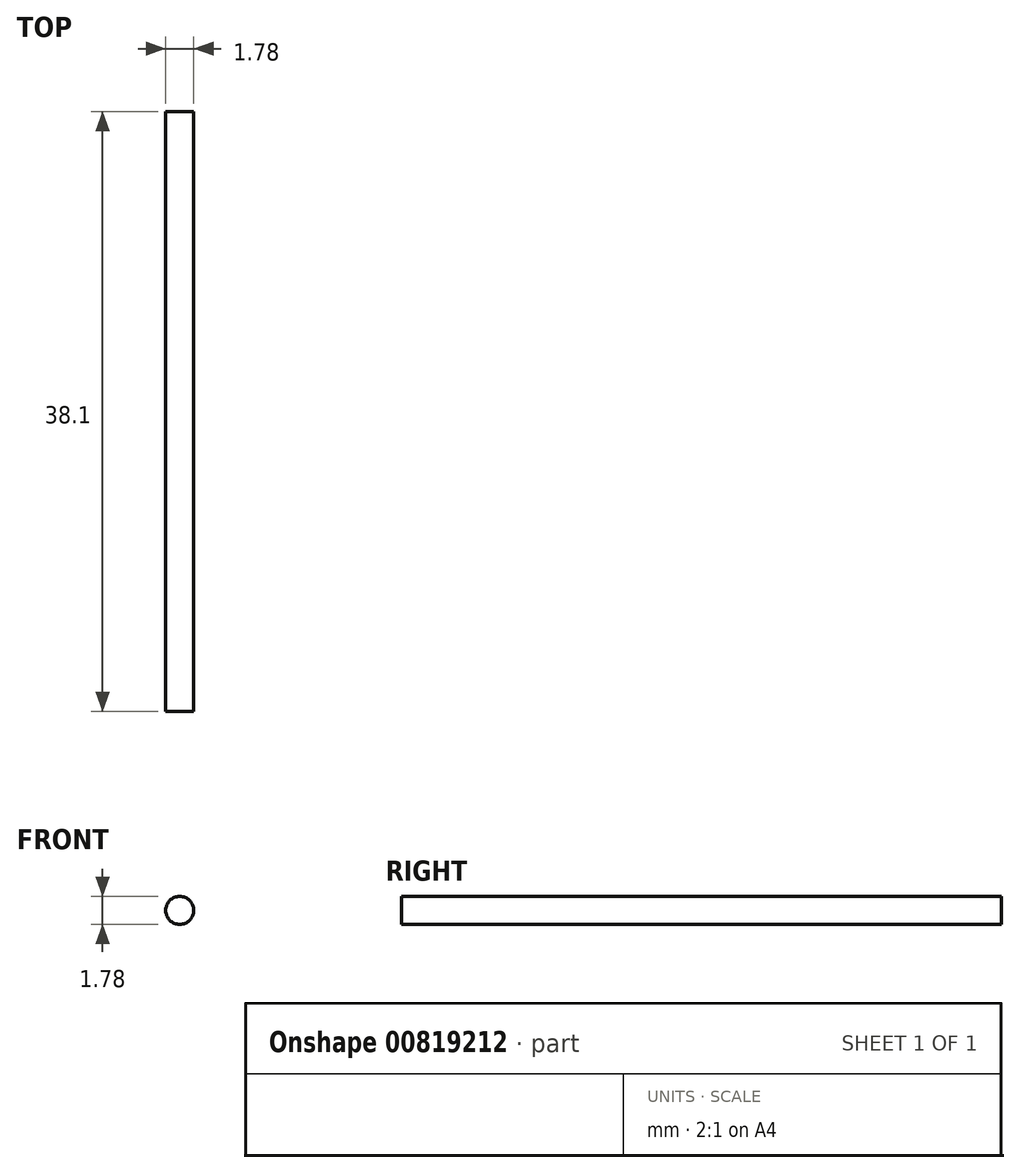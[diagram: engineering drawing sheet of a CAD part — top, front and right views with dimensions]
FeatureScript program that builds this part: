
annotation { "Feature Type Name" : "Feature", "Feature Type Description" : "" }
export const myFeature = defineFeature(function(context is Context, id is Id, definition is map)
    precondition{}
    {
        {
            var Q0;
            Q0=qCreatedBy(makeId("Front.planeOp"),FACE);
            var sketch = newSketch(context, id + "F0", { "sketchPlane" : qUnion([Q0])});
            skCircle(sketch, "E0", {"center": v(0, 0) * mm, "radius": 0.89 * mm});
            skSolve(sketch);
        }
        {
            var Q0;
            Q0=makeQuery(id+"F0.imprint","IMPRINT",FACE,{"disambiguationData":[TD([[makeQuery(id+"F0.imprint","IMPRINT",EDGE,{"derivedFrom":sQuery(id+"F0.wireOp",EDGE,"E0")}),1.0]])]});
            extrude(context, id + "F1", {"entities" : qUnion([Q0]), "depth" : 38.1 * mm, "offsetDistance" : 25.4 * mm});
        }
    });
